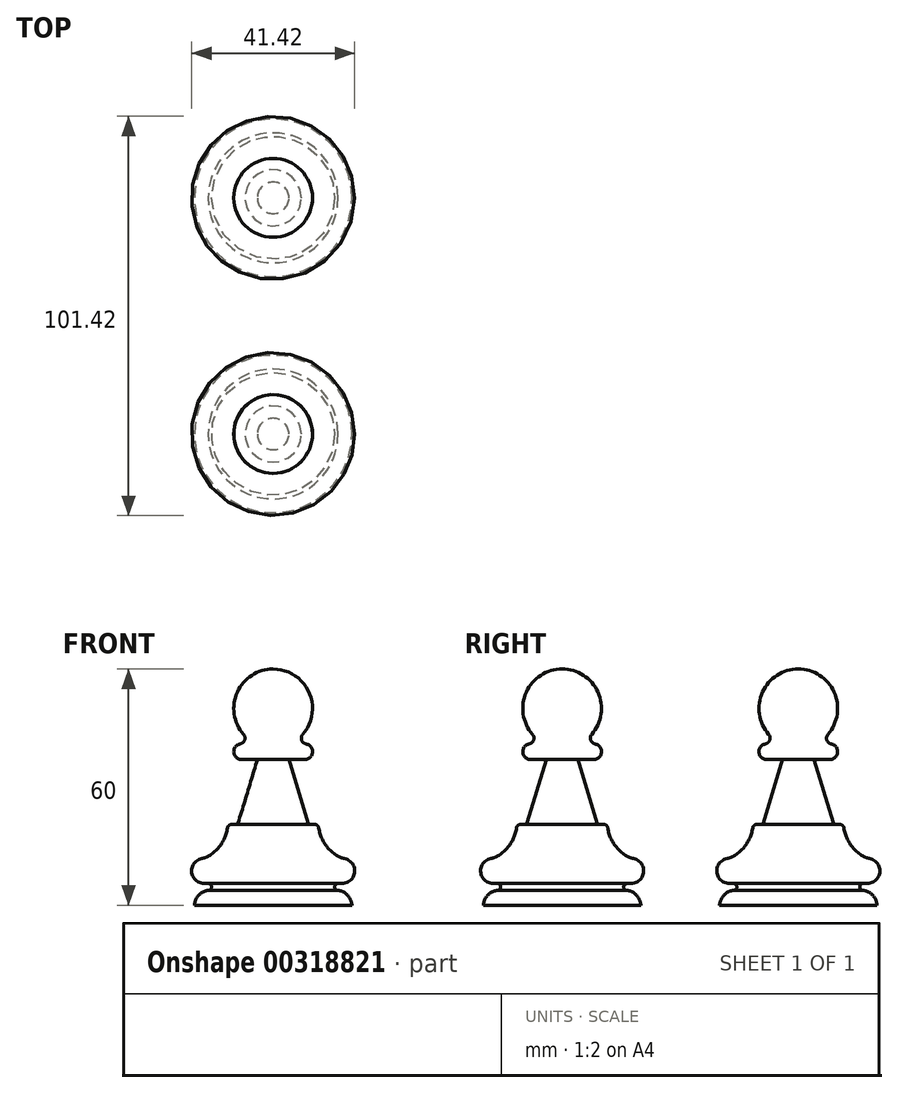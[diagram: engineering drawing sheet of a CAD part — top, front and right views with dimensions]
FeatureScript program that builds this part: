
annotation { "Feature Type Name" : "Feature", "Feature Type Description" : "" }
export const myFeature = defineFeature(function(context is Context, id is Id, definition is map)
    precondition{}
    {
        {
            var Q0;
            Q0=qCreatedBy(makeId("Front.planeOp"),FACE);
            var sketch = newSketch(context, id + "F0", { "sketchPlane" : qUnion([Q0])});
            skArc(sketch, "E0", {"start": v(0, 19.5) * mm, "mid": v(-10, 9.5) * mm, "end": v(0, -0.5) * mm});
            skLineSegment(sketch, "E1", {"start": v(0, 0.5) * mm, "end": v(-8, 0.5) * mm});
            skLineSegment(sketch, "E2", {"start": v(0, -3.5) * mm, "end": v(-8, -3.5) * mm});
            skArc(sketch, "E3", {"start": v(-8, 0.5) * mm, "mid": v(-10, -1.5) * mm, "end": v(-8, -3.5) * mm});
            skLineSegment(sketch, "E4", {"start": v(-4, -3.5) * mm, "end": v(-9, -20) * mm});
            skLineSegment(sketch, "E5", {"start": v(-9, -20) * mm, "end": v(-11.5, -20) * mm});
            skArc(sketch, "E6", {"start": v(-17.5, -28.59) * mm, "mid": v(-13.29, -25.14) * mm, "end": v(-11.5, -20) * mm});
            skArc(sketch, "E7", {"start": v(-17.5, -28.59) * mm, "mid": v(-20.7, -31.8) * mm, "end": v(-17.5, -35) * mm});
            skLineSegment(sketch, "E8", {"start": v(-17.5, -35) * mm, "end": v(-16.5, -35) * mm});
            skArc(sketch, "E9", {"start": v(-16.5, -36.75) * mm, "mid": v(-15.63, -35.88) * mm, "end": v(-16.5, -35) * mm});
            skArc(sketch, "E10", {"start": v(-16.5, -36.75) * mm, "mid": v(-18.93, -38) * mm, "end": v(-20, -40.5) * mm});
            skLineSegment(sketch, "E11", {"start": v(-20, -40.5) * mm, "end": v(0, -40.5) * mm});
            skLineSegment(sketch, "E12", {"start": v(0, -40.5) * mm, "end": v(0, 19.5) * mm});
            skLineSegment(sketch, "E13", {"start": v(0, 40.56) * mm, "end": v(0, -79.2) * mm, "construction": true});
            skSolve(sketch);
        }
        {
            var Q0;
            {var subQ0=sQuery(id+"F0.wireOp",EDGE,"E3");Q0=makeQuery(id+"F0.imprint","IMPRINT",FACE,{"disambiguationData":[TD([[makeQuery(id+"F0.imprint","IMPRINT",EDGE,{"derivedFrom":subQ0}),1.0]])]});}
            var Q1;
            {var subQ0=sQuery(id+"F0.wireOp",EDGE,"E4");Q1=makeQuery(id+"F0.imprint","IMPRINT",FACE,{"disambiguationData":[TD([[makeQuery(id+"F0.imprint","IMPRINT",EDGE,{"derivedFrom":subQ0}),1.0]])]});}
            var Q2;
            {var subQ0=sQuery(id+"F0.wireOp",EDGE,"E12");var subQ1=sQuery(id+"F0.wireOp",EDGE,"E0");var subQ2=makeQuery(id+"F0.imprint","INTERSECT",VERTEX,{"disambiguationData":[OD(0.0)],"derivedFrom":[subQ1,subQ0]});Q2=makeQuery(id+"F0.imprint","IMPRINT",FACE,{"disambiguationData":[TD([[makeQuery(id+"F0.imprint","IMPRINT",EDGE,{"disambiguationData":[TD([[subQ2,-1.0]])],"derivedFrom":subQ1}),1.0]])]});}
            var Q3;
            {var subQ0=sQuery(id+"F0.wireOp",EDGE,"E12");var subQ1=sQuery(id+"F0.wireOp",EDGE,"E0");var subQ2=makeQuery(id+"F0.imprint","INTERSECT",VERTEX,{"disambiguationData":[OD(1.0)],"derivedFrom":[subQ1,subQ0]});Q3=makeQuery(id+"F0.imprint","IMPRINT",FACE,{"disambiguationData":[TD([[makeQuery(id+"F0.imprint","IMPRINT",EDGE,{"disambiguationData":[TD([[subQ2,1.0]])],"derivedFrom":subQ1}),1.0]])]});}
            var Q4;
            Q4=sQuery(id+"F0.wireOp",EDGE,"E13");
            revolve(context, id + "F1", {"entities" : qUnion([Q0, Q1, Q2, Q3]), "axis" : qUnion([Q4]), "revolveType" : RevolveType.FULL});
        }
        {
            var Q0;
            Q0=makeQuery(id+"F1.opRevolve","SWEPT_EDGE",EDGE,{"disambiguationData":[OSD([sQuery(id+"F0.wireOp",EDGE,"E0"),sQuery(id+"F0.wireOp",EDGE,"E1")])]});
            fillet(context, id + "F2", {"entities" : qUnion([Q0]), "radius" : 1.5 * mm, "tangentPropagation" : true, "allowEdgeOverflow" : false});
        }
        {
            var Q0;
            Q0=makeQuery(id+"F1.opRevolve","SWEPT_EDGE",EDGE,{"disambiguationData":[OSD([sQuery(id+"F0.wireOp",EDGE,"E5"),sQuery(id+"F0.wireOp",EDGE,"E6")])]});
            fillet(context, id + "F3", {"entities" : qUnion([Q0]), "radius" : 1 * mm, "tangentPropagation" : true, "allowEdgeOverflow" : false});
        }
        {
            var Q0;
            Q0=makeQuery(id+"F1.opRevolve","SWEPT_EDGE",EDGE,{"disambiguationData":[OSD([sQuery(id+"F0.wireOp",EDGE,"E4"),sQuery(id+"F0.wireOp",EDGE,"E5")])]});
            fillet(context, id + "F4", {"entities" : qUnion([Q0]), "radius" : 0.5 * mm, "tangentPropagation" : true, "allowEdgeOverflow" : false});
        }
        {
            var Q0;
            Q0=makeQuery(id+"F1.opRevolve","SWEPT_EDGE",EDGE,{"disambiguationData":[OSD([sQuery(id+"F0.wireOp",EDGE,"E6"),sQuery(id+"F0.wireOp",EDGE,"E7")])]});
            var Q1;
            Q1=makeQuery(id+"F1.opRevolve","SWEPT_EDGE",EDGE,{"disambiguationData":[OSD([sQuery(id+"F0.wireOp",EDGE,"E7"),sQuery(id+"F0.wireOp",EDGE,"E8")])]});
            var Q2;
            Q2=makeQuery(id+"F1.opRevolve","SWEPT_EDGE",EDGE,{"disambiguationData":[OSD([sQuery(id+"F0.wireOp",EDGE,"E8"),sQuery(id+"F0.wireOp",EDGE,"E9")])]});
            fillet(context, id + "F5", {"entities" : qUnion([Q0, Q1, Q2]), "radius" : 5 * mm, "tangentPropagation" : true, "allowEdgeOverflow" : false});
        }
        {
            var Q0;
            Q0=qCreatedBy(makeId("Front.planeOp"),FACE);
            cPlane(context, id + "F6", {"entities" : qUnion([Q0]), "cplaneType" : CPlaneType.OFFSET, "offset" : 30 * mm, "width" : 150 * mm, "height" : 150 * mm});
        }
        {
            var Q0;
            Q0=makeQuery(id+"F1.opRevolve","SWEPT_BODY",BODY,{"disambiguationData":[OSD([sQuery(id+"F0.wireOp",EDGE,"E0"),sQuery(id+"F0.wireOp",EDGE,"E1"),sQuery(id+"F0.wireOp",EDGE,"E2"),sQuery(id+"F0.wireOp",EDGE,"E3"),sQuery(id+"F0.wireOp",EDGE,"E4"),sQuery(id+"F0.wireOp",EDGE,"E5"),sQuery(id+"F0.wireOp",EDGE,"E6"),sQuery(id+"F0.wireOp",EDGE,"E7"),sQuery(id+"F0.wireOp",EDGE,"E8"),sQuery(id+"F0.wireOp",EDGE,"E9"),sQuery(id+"F0.wireOp",EDGE,"E10"),sQuery(id+"F0.wireOp",EDGE,"E11"),sQuery(id+"F0.wireOp",EDGE,"E12")])]});
            var Q1;
            Q1=qCreatedBy(id+"F6.planeOp",FACE);
            mirror(context, id + "F7", {"entities" : qUnion([Q0]), "mirrorPlane" : qUnion([Q1])});
        }
    });
